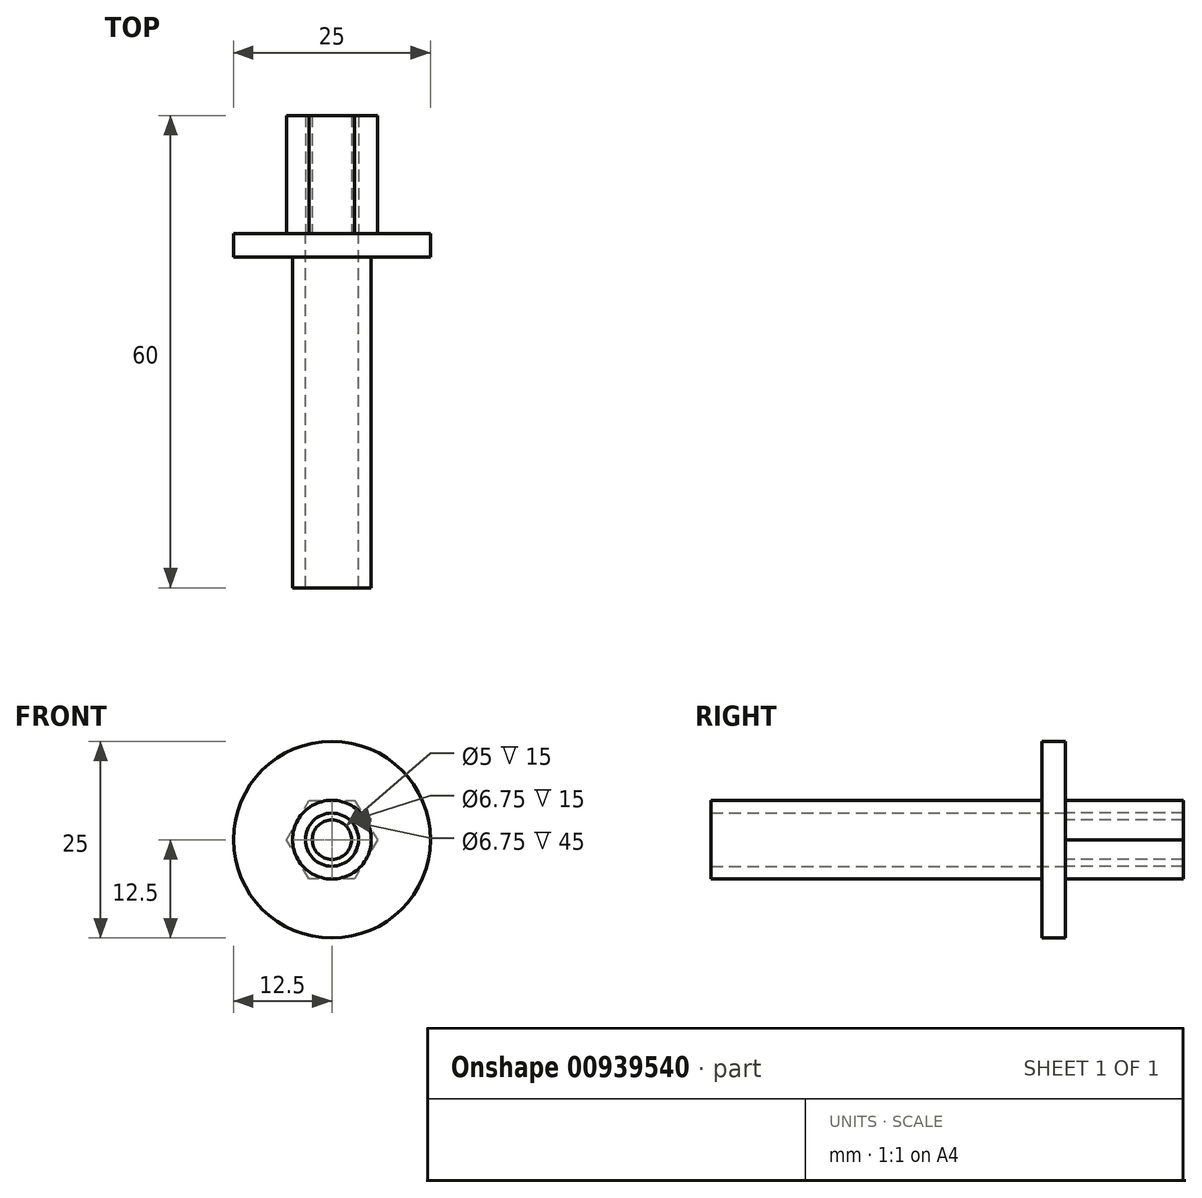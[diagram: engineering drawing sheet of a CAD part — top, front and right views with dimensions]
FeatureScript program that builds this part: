
annotation { "Feature Type Name" : "Feature", "Feature Type Description" : "" }
export const myFeature = defineFeature(function(context is Context, id is Id, definition is map)
    precondition{}
    {
        {
            var Q0;
            Q0=qCreatedBy(makeId("Front.planeOp"),FACE);
            var sketch = newSketch(context, id + "F0", { "sketchPlane" : qUnion([Q0])});
            skLineSegment(sketch, "E0", {"start": v(0.89, 64.83) * mm, "end": v(-0.69, -50.12) * mm, "construction": true});
            skCircle(sketch, "E1", {"center": v(0, 0) * mm, "radius": 12.5 * mm});
            skCircle(sketch, "E2", {"center": v(0, 0) * mm, "radius": 3.38 * mm});
            skArc(sketch, "E3.cCircle", {"start": v(-0.07, -5) * mm, "mid": v(-0.03, -5) * mm, "end": v(0, -5) * mm, "construction": true});
            skLineSegment(sketch, "E3.0", {"start": v(5.77, 0) * mm, "end": v(2.89, -5) * mm});
            skLineSegment(sketch, "E3.1", {"start": v(2.89, -5) * mm, "end": v(-2.89, -5) * mm});
            skLineSegment(sketch, "E3.2", {"start": v(-2.89, -5) * mm, "end": v(-5.77, 0) * mm});
            skLineSegment(sketch, "E3.3", {"start": v(-5.77, 0) * mm, "end": v(-2.89, 5) * mm});
            skLineSegment(sketch, "E3.4", {"start": v(-2.89, 5) * mm, "end": v(2.89, 5) * mm});
            skLineSegment(sketch, "E3.5", {"start": v(2.89, 5) * mm, "end": v(5.77, 0) * mm});
            skPoint(sketch, "E3.0.midPoint", {"position": v(4.33, -2.5) * mm});
            skCircle(sketch, "E4", {"center": v(0, 0) * mm, "radius": 2.5 * mm});
            skArc(sketch, "E5.trimOffspring", {"start": v(0.07, 5) * mm, "mid": v(0.03, 5) * mm, "end": v(0, 5) * mm, "construction": true});
            skSolve(sketch);
        }
        {
            var Q0;
            Q0=makeQuery(id+"F0.imprint","IMPRINT",FACE,{"disambiguationData":[TD([[makeQuery(id+"F0.imprint","IMPRINT",EDGE,{"derivedFrom":sQuery(id+"F0.wireOp",EDGE,"E2")}),-1.0]])]});
            extrude(context, id + "F1", {"entities" : qUnion([Q0]), "depth" : 45 * mm, "offsetDistance" : 25 * mm});
        }
        {
            var Q0;
            Q0=makeQuery(id+"F0.imprint","IMPRINT",FACE,{"disambiguationData":[TD([[makeQuery(id+"F0.imprint","IMPRINT",EDGE,{"derivedFrom":sQuery(id+"F0.wireOp",EDGE,"E1")}),1.0]])]});
            var Q1;
            Q1=makeQuery(id+"F0.imprint","IMPRINT",FACE,{"disambiguationData":[TD([[makeQuery(id+"F0.imprint","IMPRINT",EDGE,{"derivedFrom":sQuery(id+"F0.wireOp",EDGE,"E2")}),-1.0]])]});
            extrude(context, id + "F2", {"entities" : qUnion([Q0, Q1]), "operationType" : NewBodyOperationType.ADD, "depth" : 3 * mm, "offsetDistance" : 25 * mm});
        }
        {
            var Q0;
            Q0=makeQuery(id+"F0.imprint","IMPRINT",FACE,{"disambiguationData":[TD([[makeQuery(id+"F0.imprint","IMPRINT",EDGE,{"derivedFrom":sQuery(id+"F0.wireOp",EDGE,"E3.0")}),-1.0]])]});
            var Q1;
            Q1=sQuery(id+"F0.wireOp",EDGE,"E4");
            extrude(context, id + "F3", {"entities" : qUnion([Q0]), "surfaceEntities" : qUnion([Q1]), "depth" : -15 * mm, "offsetDistance" : 25 * mm});
        }
        {
            var Q0;
            Q0=makeQuery(id+"F1.opExtrude","SWEPT_EDGE",EDGE,{"disambiguationData":[OSD([sQuery(id+"F0.wireOp",EDGE,"E3.0"),sQuery(id+"F0.wireOp",EDGE,"E3.1")])]});
            fillet(context, id + "F4", {"entities" : qUnion([Q0]), "radius" : 5 * mm, "tangentPropagation" : true, "allowEdgeOverflow" : false});
        }
        {
            var Q0;
            Q0=makeQuery(id+"F1.opExtrude","SWEPT_EDGE",EDGE,{"disambiguationData":[OSD([sQuery(id+"F0.wireOp",EDGE,"E3.1"),sQuery(id+"F0.wireOp",EDGE,"E3.2")])]});
            fillet(context, id + "F5", {"entities" : qUnion([Q0]), "radius" : 5 * mm, "tangentPropagation" : true, "allowEdgeOverflow" : false});
        }
        {
            var Q0;
            Q0=makeQuery(id+"F1.opExtrude","SWEPT_EDGE",EDGE,{"disambiguationData":[OSD([sQuery(id+"F0.wireOp",EDGE,"E3.2"),sQuery(id+"F0.wireOp",EDGE,"E3.3")])]});
            fillet(context, id + "F6", {"entities" : qUnion([Q0]), "radius" : 5 * mm, "tangentPropagation" : true, "allowEdgeOverflow" : false});
        }
        {
            var Q0;
            Q0=makeQuery(id+"F1.opExtrude","SWEPT_EDGE",EDGE,{"disambiguationData":[OSD([sQuery(id+"F0.wireOp",EDGE,"E3.3"),sQuery(id+"F0.wireOp",EDGE,"E3.4")])]});
            fillet(context, id + "F7", {"entities" : qUnion([Q0]), "radius" : 5 * mm, "tangentPropagation" : true, "allowEdgeOverflow" : false});
        }
        {
            var Q0;
            Q0=makeQuery(id+"F1.opExtrude","SWEPT_EDGE",EDGE,{"disambiguationData":[OSD([sQuery(id+"F0.wireOp",EDGE,"E3.0"),sQuery(id+"F0.wireOp",EDGE,"E3.5")])]});
            fillet(context, id + "F8", {"entities" : qUnion([Q0]), "radius" : 5 * mm, "tangentPropagation" : true, "allowEdgeOverflow" : false});
        }
        {
            var Q0;
            Q0=makeQuery(id+"F1.opExtrude","SWEPT_EDGE",EDGE,{"disambiguationData":[OSD([sQuery(id+"F0.wireOp",EDGE,"E3.4"),sQuery(id+"F0.wireOp",EDGE,"E3.5")])]});
            fillet(context, id + "F9", {"entities" : qUnion([Q0]), "radius" : 5 * mm, "tangentPropagation" : true, "allowEdgeOverflow" : false});
        }
        {
            var Q0;
            Q0=makeQuery(id+"F0.imprint","IMPRINT",FACE,{"disambiguationData":[TD([[makeQuery(id+"F0.imprint","IMPRINT",EDGE,{"derivedFrom":sQuery(id+"F0.wireOp",EDGE,"E4")}),-1.0]])]});
            extrude(context, id + "F10", {"entities" : qUnion([Q0]), "depth" : -15 * mm, "offsetDistance" : 25 * mm});
        }
    });
